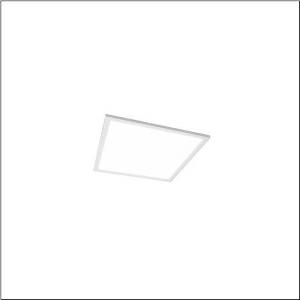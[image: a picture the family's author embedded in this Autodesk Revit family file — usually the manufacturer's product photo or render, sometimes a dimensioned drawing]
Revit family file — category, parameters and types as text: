
# Revit family: apollon_r__21_square_51mq13wd2413_7426
name_source: partatom
category: Lighting Fixtures
units: mm (PartAtom-declared; Revit-internal decimal feet)

## family parameters
Cut with Voids When Loaded = No
Host = Face
Light Source = No
Part Type = Normal
Room Calculation Point = No
Round Connector Dimension = Use Diameter
Shared = No

## types (1)
- Apollon® 21 square (1 x LED, 1800 lm, 15 W, 4000K)
    Apparent Load = 15 VA
    CIE Flux Codes = 59 88 97 100 100
    Color Rendering = 80
    Color Temperature = 4000K
    Default Elevation = 1800 mm  [stored 5.90551 ft]
    Description = Apollon® 21 square, office luminaire, primary optical cover: micro prismatic cover, of PMMA, CAT 2 (L<= 3000cd/m²), light emission: direct distribution, primary light characteristic: symmetric, installation type: lay-in mounting, LED, rated luminous flux: 1.800lm, luminous efficacy: 120lm/W, light colour: 840, colour temperature: 4000K, control gear: ECG DALI, with terminal, 5-pole, mains connection: 220..240V, AC, 50/60Hz, rated input power: 15W, housing, of sheet steel, coated, pure white, length: 296mm, width: 296mm, height: 40mm, housing upper side, of sheet steel, galvanised, protection rating (complete): IP20, protection rating (lamp compartment, on room side): IP50, insulation class (complete): insulation class II (safety insulation), certification: CE, ENEC, permissible operating ambient temperature: -20..+40°C, packaging unit: 1 piece
    Height = 0 mm  [stored 0 ft]
    Lamp = 1 x LED
    Lamp Light Flux = 1800 lm
    Lamp Power = 15 W
    Lamp count = 1
    Length = 295 mm
    Luminous efficacy = 120 lm/W
    Manufacturer = Siteco
    ModVariant = No
    Model = 51MQ13WD2413
    Mounting Place = Ceiling
    Mounting Type = Recessed
    Number of Poles = 1
    OnlyDefault = Yes
    Power Factor = 1
    Product Name = Apollon® 21 square
    Product group = office luminaire | ceiling recessed
    ProductGroupID = 400
    Protection Class = Protection class II
    Protection Degree = IP 20
    RLX_Detail_Level = 1
    RlxData = <blob elided: 10737 chars, md5=16a7ebc9>
    Socket = socket
    Standby Power = 0 W
    System Light Flux = 1800 lm
    System Power = 15 W
    Type Comments = Product without accessories
    Type Image = l_1006815.jpg
    URL = http://relux.com
    VarID = ---
    Voltage = 0 V
    Weight = 0.00 kg
    Width = 295 mm

note: [stored X ft] marks values corroborated as IEEE doubles in the binary element streams (Revit-internal decimal feet)

## geometry (parser evidence)
native form markers: Sweep x9
no freeform markers — native parametric forms only
